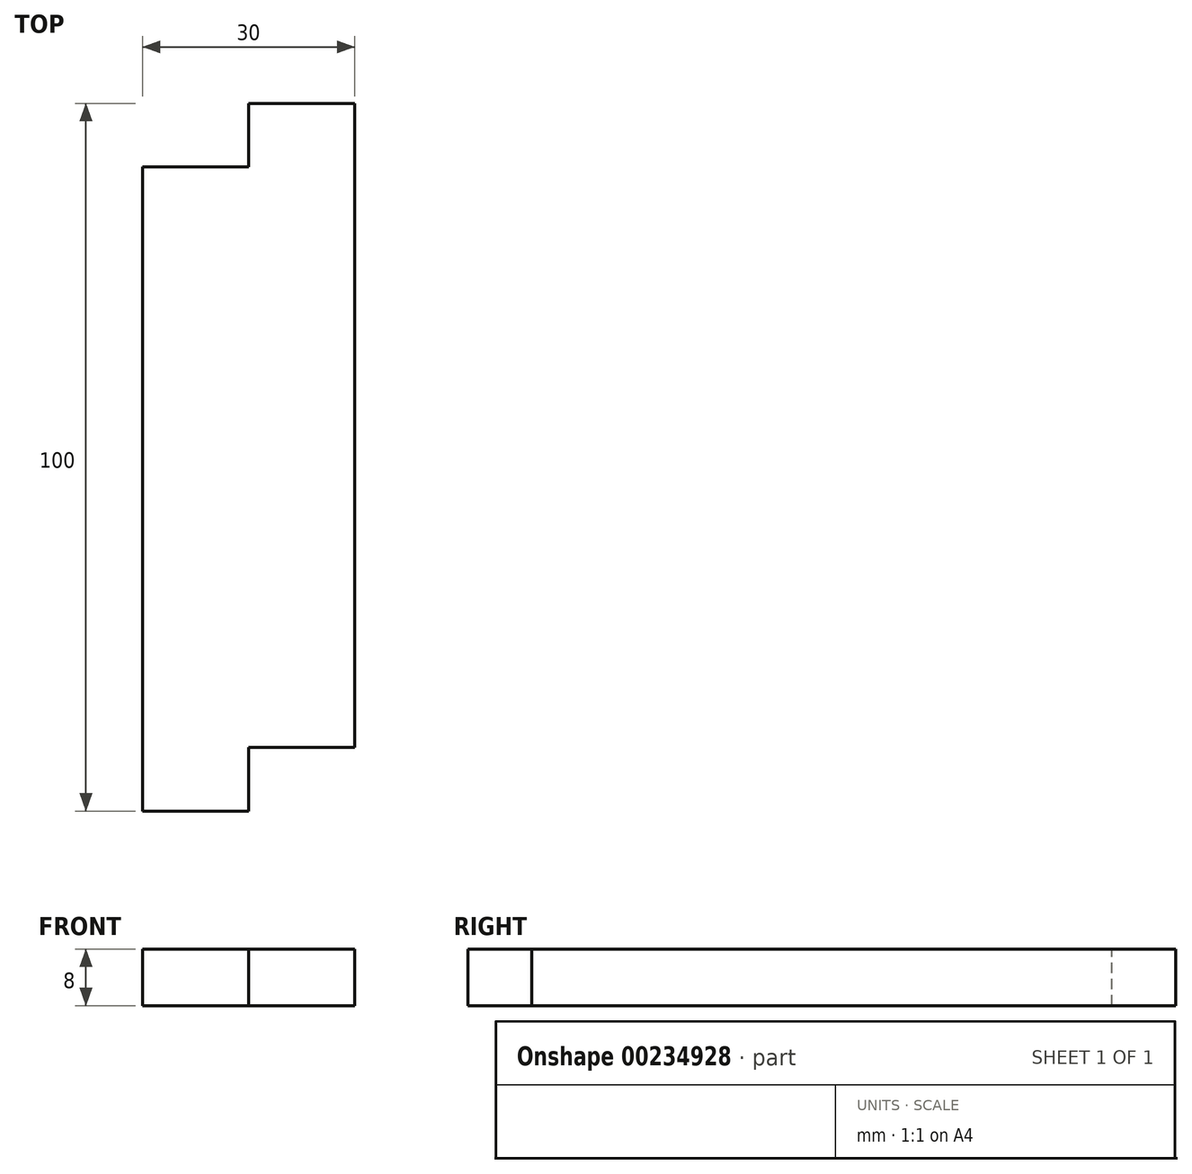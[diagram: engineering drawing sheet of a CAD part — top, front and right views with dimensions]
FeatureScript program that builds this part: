
annotation { "Feature Type Name" : "Feature", "Feature Type Description" : "" }
export const myFeature = defineFeature(function(context is Context, id is Id, definition is map)
    precondition{}
    {
        {
            var Q0;
            Q0=qCreatedBy(makeId("Top.planeOp"),FACE);
            var sketch = newSketch(context, id + "F0", { "sketchPlane" : qUnion([Q0])});
            skLineSegment(sketch, "E0.bottom", {"start": v(21, 60) * mm, "end": v(-21, 60) * mm});
            skLineSegment(sketch, "E0.top", {"start": v(21, -60) * mm, "end": v(-21, -60) * mm});
            skLineSegment(sketch, "E0.left", {"start": v(21, 60) * mm, "end": v(21, -60) * mm});
            skLineSegment(sketch, "E0.right", {"start": v(-21, 60) * mm, "end": v(-21, -60) * mm});
            skPoint(sketch, "E0.middle", {"position": v(0, 0) * mm});
            skSolve(sketch);
        }
        {
            var Q0;
            Q0=qSketchRegion(id+"F0",true);
            extrude(context, id + "F1", {"entities" : qUnion([Q0]), "depth" : 8 * mm, "offsetDistance" : 25 * mm});
        }
        {
            var Q0;
            Q0=makeQuery(id+"F1.opExtrude","CAP_FACE",FACE,{"disambiguationData":[OSD([sQuery(id+"F0.wireOp",EDGE,"E0.bottom"),sQuery(id+"F0.wireOp",EDGE,"E0.top"),sQuery(id+"F0.wireOp",EDGE,"E0.left"),sQuery(id+"F0.wireOp",EDGE,"E0.right")])],"isStart":false});
            var sketch = newSketch(context, id + "F2", { "sketchPlane" : qUnion([Q0])});
            skLineSegment(sketch, "E1.bottom", {"start": v(15, 50) * mm, "end": v(-15, 50) * mm});
            skLineSegment(sketch, "E1.top", {"start": v(15, -50) * mm, "end": v(-15, -50) * mm});
            skLineSegment(sketch, "E1.left", {"start": v(15, 50) * mm, "end": v(15, -50) * mm});
            skLineSegment(sketch, "E1.right", {"start": v(-15, 50) * mm, "end": v(-15, -50) * mm});
            skPoint(sketch, "E1.middle", {"position": v(0, 0) * mm});
            skLineSegment(sketch, "E2.bottom", {"start": v(21, 60) * mm, "end": v(-21, 60) * mm});
            skLineSegment(sketch, "E2.top", {"start": v(21, -60) * mm, "end": v(-21, -60) * mm});
            skLineSegment(sketch, "E2.left", {"start": v(21, 60) * mm, "end": v(21, -60) * mm});
            skLineSegment(sketch, "E2.right", {"start": v(-21, 60) * mm, "end": v(-21, -60) * mm});
            skSolve(sketch);
        }
        {
            var Q0;
            Q0 = qSketchRegion(id + "F2", true);
            extrude(context, id + "F3", {"entities" : qUnion([Q0]), "operationType" : NewBodyOperationType.REMOVE, "oppositeDirection" : true, "depth" : 25 * mm, "offsetDistance" : 25 * mm});
        }
        {
            var Q0;
            Q0=makeQuery(id+"F1.opExtrude","CAP_FACE",FACE,{"disambiguationData":[OSD([sQuery(id+"F0.wireOp",EDGE,"E0.bottom"),sQuery(id+"F0.wireOp",EDGE,"E0.top"),sQuery(id+"F0.wireOp",EDGE,"E0.left"),sQuery(id+"F0.wireOp",EDGE,"E0.right")])],"isStart":false});
            var sketch = newSketch(context, id + "F4", { "sketchPlane" : qUnion([Q0])});
            skLineSegment(sketch, "E3", {"start": v(0, 50) * mm, "end": v(0, -50) * mm, "construction": true});
            skLineSegment(sketch, "E4", {"start": v(-15, 0) * mm, "end": v(15, 0) * mm, "construction": true});
            skLineSegment(sketch, "E5", {"start": v(-15, 40) * mm, "end": v(15, 40) * mm});
            skLineSegment(sketch, "E6", {"start": v(-15, -40) * mm, "end": v(15, -40) * mm});
            skLineSegment(sketch, "E7", {"start": v(0, 50) * mm, "end": v(0, 40) * mm});
            skLineSegment(sketch, "E8", {"start": v(0, -50) * mm, "end": v(0, -40) * mm});
            skLineSegment(sketch, "E9", {"start": v(0, 50) * mm, "end": v(-15, 50) * mm});
            skLineSegment(sketch, "E10", {"start": v(-15, 50) * mm, "end": v(-15, 40) * mm});
            skLineSegment(sketch, "E11", {"start": v(15, -50) * mm, "end": v(15, -40) * mm});
            skSolve(sketch);
        }
        {
            var Q0;
            Q0 = qSketchRegion(id + "F4", true);
            var Q1;
            {var subQ2=sQuery(id+"F4.wireOp",EDGE,"E8");Q1=makeQuery(id+"F4.imprint","IMPRINT",FACE,{"disambiguationData":[TD([[makeQuery(id+"F4.imprint","IMPRINT",EDGE,{"derivedFrom":subQ2}),-1.0]])]});}
            extrude(context, id + "F5", {"entities" : qUnion([Q0, Q1]), "operationType" : NewBodyOperationType.REMOVE, "oppositeDirection" : true, "depth" : 25 * mm, "offsetDistance" : 25 * mm});
        }
        {
            var Q0;
            Q0=makeQuery(id+"F5.boolean.opBoolean","COPY",FACE,{"derivedFrom":makeQuery(id+"F5.opExtrude","SWEPT_FACE",FACE,{"disambiguationData":[OSD([sQuery(id+"F4.wireOp",EDGE,"E5")])]})});
            extrude(context, id + "F6", {"entities" : qUnion([Q0]), "operationType" : NewBodyOperationType.ADD, "depth" : 1 * mm, "offsetDistance" : 25 * mm});
        }
        {
            var Q0;
            Q0=makeQuery(id+"F5.boolean.opBoolean","COPY",FACE,{"derivedFrom":makeQuery(id+"F5.opExtrude","SWEPT_FACE",FACE,{"disambiguationData":[OSD([sQuery(id+"F4.wireOp",EDGE,"E6")])]})});
            extrude(context, id + "F7", {"entities" : qUnion([Q0]), "operationType" : NewBodyOperationType.ADD, "depth" : 1 * mm, "offsetDistance" : 25 * mm});
        }
        {
            var Q0;
            Q0=makeQuery(id+"F7.boolean.opBoolean","MERGE",FACE,{"derivedFrom":[makeQuery(id+"F6.boolean.opBoolean","MERGE",FACE,{"derivedFrom":[makeQuery(id+"F1.opExtrude","CAP_FACE",FACE,{"disambiguationData":[OSD([sQuery(id+"F0.wireOp",EDGE,"E0.bottom"),sQuery(id+"F0.wireOp",EDGE,"E0.top"),sQuery(id+"F0.wireOp",EDGE,"E0.left"),sQuery(id+"F0.wireOp",EDGE,"E0.right")])],"isStart":false}),makeQuery(id+"F6.opExtrude","SWEPT_FACE",FACE,{"disambiguationData":[OSD([sQuery(id+"F4.wireOp",EDGE,"E5")])]})]}),makeQuery(id+"F7.opExtrude","SWEPT_FACE",FACE,{"disambiguationData":[OSD([sQuery(id+"F4.wireOp",EDGE,"E6")])]})]});
            var sketch = newSketch(context, id + "F8", { "sketchPlane" : qUnion([Q0])});
            skLineSegment(sketch, "E12", {"start": v(0, 41) * mm, "end": v(0, -41) * mm, "construction": true});
            skLineSegment(sketch, "E13", {"start": v(9, 50) * mm, "end": v(9, -41) * mm, "construction": true});
            skLineSegment(sketch, "E14", {"start": v(-9, 41) * mm, "end": v(-9, -50) * mm, "construction": true});
            skCircle(sketch, "E15", {"center": v(9, 46) * mm, "radius": 1.75 * mm});
            skCircle(sketch, "E16", {"center": v(-9, -46) * mm, "radius": 1.75 * mm});
            skLineSegment(sketch, "E17", {"start": v(0, 0) * mm, "end": v(15, 0) * mm, "construction": true});
            skCircle(sketch, "E18", {"center": v(0, 26) * mm, "radius": 4.25 * mm});
            skCircle(sketch, "E19", {"center": v(0, -26) * mm, "radius": 4.25 * mm});
            skSolve(sketch);
        }
        {
            var Q0;
            Q0 = qSketchRegion(id + "F8", true);
            extrude(context, id + "F9", {"entities" : qUnion([Q0]), "operationType" : NewBodyOperationType.REMOVE, "oppositeDirection" : true, "depth" : 25 * mm, "offsetDistance" : 25 * mm});
        }
    });
